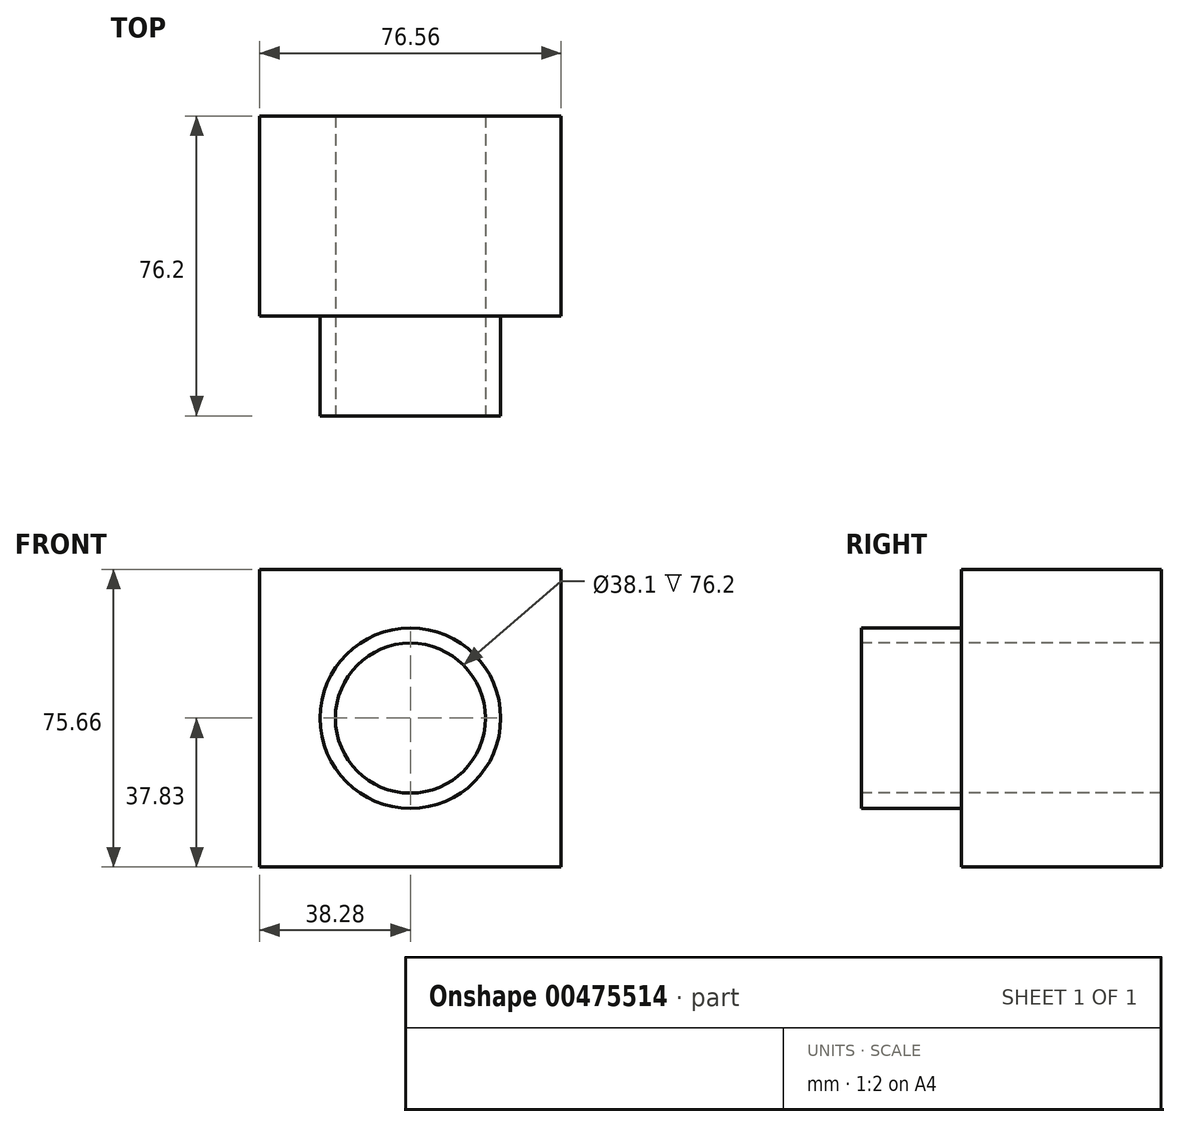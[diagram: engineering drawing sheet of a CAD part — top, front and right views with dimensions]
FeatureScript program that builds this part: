
annotation { "Feature Type Name" : "Feature", "Feature Type Description" : "" }
export const myFeature = defineFeature(function(context is Context, id is Id, definition is map)
    precondition{}
    {
        {
            var Q0;
            Q0=qCreatedBy(makeId("Front.planeOp"),FACE);
            var sketch = newSketch(context, id + "F0", { "sketchPlane" : qUnion([Q0])});
            skLineSegment(sketch, "E0.bottom", {"start": v(-38.28, 37.83) * mm, "end": v(38.28, 37.83) * mm});
            skLineSegment(sketch, "E0.top", {"start": v(-38.28, -37.83) * mm, "end": v(38.28, -37.83) * mm});
            skLineSegment(sketch, "E0.left", {"start": v(-38.28, 37.83) * mm, "end": v(-38.28, -37.83) * mm});
            skLineSegment(sketch, "E0.right", {"start": v(38.28, 37.83) * mm, "end": v(38.28, -37.83) * mm});
            skPoint(sketch, "E0.middle", {"position": v(0, 0) * mm});
            skSolve(sketch);
        }
        {
            var Q0;
            Q0=makeQuery(id+"F0.imprint","IMPRINT",FACE,{"disambiguationData":[TD([[makeQuery(id+"F0.imprint","IMPRINT",EDGE,{"derivedFrom":sQuery(id+"F0.wireOp",EDGE,"E0.bottom")}),-1.0]])]});
            extrude(context, id + "F1", {"entities" : qUnion([Q0]), "depth" : 25.4 * mm});
        }
        {
            var Q0;
            Q0=makeQuery(id+"F1.opExtrude","SWEPT_BODY",BODY,{"disambiguationData":[OSD([sQuery(id+"F0.wireOp",EDGE,"E0.bottom"),sQuery(id+"F0.wireOp",EDGE,"E0.top"),sQuery(id+"F0.wireOp",EDGE,"E0.left"),sQuery(id+"F0.wireOp",EDGE,"E0.right")])]});
            var Q1;
            Q1=makeQuery(id+"F1.opExtrude","CAP_FACE",FACE,{"disambiguationData":[OSD([sQuery(id+"F0.wireOp",EDGE,"E0.bottom"),sQuery(id+"F0.wireOp",EDGE,"E0.top"),sQuery(id+"F0.wireOp",EDGE,"E0.left"),sQuery(id+"F0.wireOp",EDGE,"E0.right")])],"isStart":false});
            mirror(context, id + "F2", {"operationType" : NewBodyOperationType.ADD, "entities" : qUnion([Q0]), "mirrorPlane" : qUnion([Q1])});
        }
        {
            var Q0;
            Q0=makeQuery(id+"F2.opPattern","COPY",FACE,{"derivedFrom":makeQuery(id+"F1.opExtrude","CAP_FACE",FACE,{"disambiguationData":[OSD([sQuery(id+"F0.wireOp",EDGE,"E0.bottom"),sQuery(id+"F0.wireOp",EDGE,"E0.top"),sQuery(id+"F0.wireOp",EDGE,"E0.left"),sQuery(id+"F0.wireOp",EDGE,"E0.right")])],"isStart":true}),"instanceName":"1"});
            var sketch = newSketch(context, id + "F3", { "sketchPlane" : qUnion([Q0])});
            skCircle(sketch, "E1", {"center": v(0, 0) * mm, "radius": 22.93 * mm});
            skSolve(sketch);
        }
        {
            var Q0;
            Q0=sQuery(id+"F3.wireOp",VERTEX,"E1.center");
            var Q1;
            Q1=makeQuery(id+"F1.opExtrude","SWEPT_BODY",BODY,{"disambiguationData":[OSD([sQuery(id+"F0.wireOp",EDGE,"E0.bottom"),sQuery(id+"F0.wireOp",EDGE,"E0.top"),sQuery(id+"F0.wireOp",EDGE,"E0.left"),sQuery(id+"F0.wireOp",EDGE,"E0.right")])]});
            hole(context, id + "F4", {"style" : HoleStyle.C_SINK, "endStyle" : HoleEndStyle.THROUGH, "holeDiameter" : 38.1 * mm, "cSinkDiameter" : 38.1 * mm, "cSinkAngle" : 90 * degree, "isTappedThrough" : true, "tappedDepth" : 12.7 * mm, "tapClearance" : 3, "locations" : qUnion([Q0]), "scope" : qUnion([Q1])});
        }
        {
            var Q0;
            Q0=makeQuery(id+"F3.imprint","IMPRINT",FACE,{"disambiguationData":[TD([[makeQuery(id+"F3.imprint","IMPRINT",EDGE,{"derivedFrom":sQuery(id+"F3.wireOp",EDGE,"E1")}),1.0]])]});
            extrude(context, id + "F5", {"entities" : qUnion([Q0]), "operationType" : NewBodyOperationType.ADD, "depth" : 25.4 * mm});
        }
        {
            var Q0;
            Q0=sQuery(id+"F3.wireOp",VERTEX,"E1.center");
            var Q1;
            Q1=makeQuery(id+"F1.opExtrude","SWEPT_BODY",BODY,{"disambiguationData":[OSD([sQuery(id+"F0.wireOp",EDGE,"E0.bottom"),sQuery(id+"F0.wireOp",EDGE,"E0.top"),sQuery(id+"F0.wireOp",EDGE,"E0.left"),sQuery(id+"F0.wireOp",EDGE,"E0.right")])]});
            hole(context, id + "F6", {"style" : HoleStyle.C_SINK, "endStyle" : HoleEndStyle.THROUGH, "oppositeDirection" : true, "holeDiameter" : 38.1 * mm, "cSinkDiameter" : 38.1 * mm, "cSinkAngle" : 90 * degree, "isTappedThrough" : true, "tappedDepth" : 12.7 * mm, "tapClearance" : 3, "locations" : qUnion([Q0]), "scope" : qUnion([Q1])});
        }
    });
